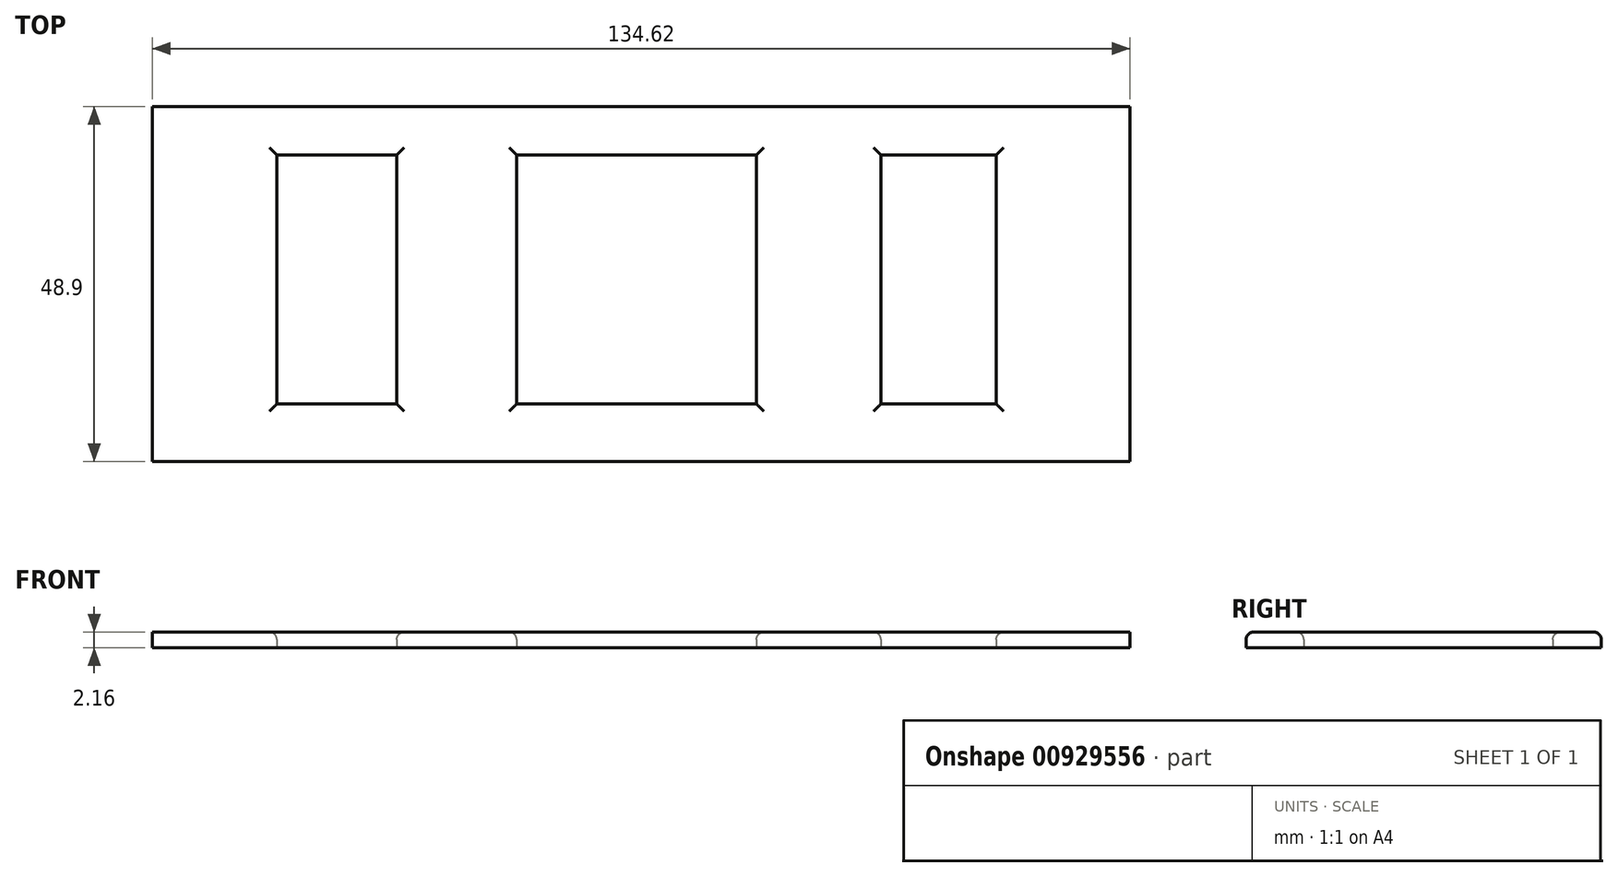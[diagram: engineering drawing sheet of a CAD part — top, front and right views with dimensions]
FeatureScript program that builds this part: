
annotation { "Feature Type Name" : "Feature", "Feature Type Description" : "" }
export const myFeature = defineFeature(function(context is Context, id is Id, definition is map)
    precondition{}
    {
        {
            var Q0;
            Q0=qCreatedBy(makeId("Top.planeOp"),FACE);
            var sketch = newSketch(context, id + "F0", { "sketchPlane" : qUnion([Q0])});
            skPoint(sketch, "E0.middle", {"position": v(0, 0) * mm});
            skLineSegment(sketch, "E1.bottom", {"start": v(-67.3, -24.45) * mm, "end": v(67.3, -24.45) * mm});
            skLineSegment(sketch, "E1.top", {"start": v(-67.3, 24.45) * mm, "end": v(67.3, 24.45) * mm});
            skLineSegment(sketch, "E1.left", {"start": v(-67.31, -24.45) * mm, "end": v(-67.3, 24.45) * mm});
            skLineSegment(sketch, "E1.right", {"start": v(67.31, -24.45) * mm, "end": v(67.31, 24.45) * mm});
            skLineSegment(sketch, "E2", {"start": v(33.02, 17.78) * mm, "end": v(33.02, -16.5) * mm});
            skLineSegment(sketch, "E3", {"start": v(67.31, 0) * mm, "end": v(67.31, 24.45) * mm});
            skLineSegment(sketch, "E4", {"start": v(67.31, 0) * mm, "end": v(67.31, -24.45) * mm});
            skLineSegment(sketch, "E5", {"start": v(-67.3, 24.45) * mm, "end": v(0, 24.45) * mm});
            skLineSegment(sketch, "E6", {"start": v(33.02, 24.45) * mm, "end": v(0, 24.45) * mm});
            skLineSegment(sketch, "E7", {"start": v(15.88, 17.78) * mm, "end": v(15.88, -16.5) * mm});
            skLineSegment(sketch, "E8", {"start": v(33.02, -24.45) * mm, "end": v(67.3, -24.45) * mm});
            skLineSegment(sketch, "E9", {"start": v(48.9, -16.5) * mm, "end": v(48.9, 17.78) * mm});
            skLineSegment(sketch, "E10", {"start": v(0, 24.45) * mm, "end": v(-67.3, 24.45) * mm});
            skLineSegment(sketch, "E11", {"start": v(-33.65, 17.78) * mm, "end": v(-33.65, -16.5) * mm});
            skLineSegment(sketch, "E12", {"start": v(-33.65, 24.45) * mm, "end": v(-67.3, 24.45) * mm});
            skLineSegment(sketch, "E13", {"start": v(-33.65, -24.45) * mm, "end": v(0, -24.45) * mm});
            skLineSegment(sketch, "E14", {"start": v(-17.14, -16.5) * mm, "end": v(-17.14, 17.78) * mm});
            skLineSegment(sketch, "E15", {"start": v(-67.31, 24.45) * mm, "end": v(-67.31, 10.48) * mm});
            skLineSegment(sketch, "E16", {"start": v(-50.16, 17.78) * mm, "end": v(-33.65, 17.78) * mm});
            skLineSegment(sketch, "E17", {"start": v(-67.31, -10.48) * mm, "end": v(-67.31, -24.45) * mm});
            skLineSegment(sketch, "E18", {"start": v(-50.16, -16.5) * mm, "end": v(-33.65, -16.5) * mm});
            skLineSegment(sketch, "E19.trimOffspring", {"start": v(-17.14, 17.78) * mm, "end": v(15.88, 17.78) * mm});
            skLineSegment(sketch, "E20.trimOffspring", {"start": v(-17.14, -16.5) * mm, "end": v(15.88, -16.5) * mm});
            skLineSegment(sketch, "E21.trimOffspring", {"start": v(33.02, 17.78) * mm, "end": v(48.9, 17.78) * mm});
            skLineSegment(sketch, "E22.trimOffspring", {"start": v(-50.16, 17.78) * mm, "end": v(-50.16, -16.5) * mm});
            skLineSegment(sketch, "E23.trimOffspring", {"start": v(33.02, -16.5) * mm, "end": v(48.9, -16.5) * mm});
            skSolve(sketch);
        }
        {
            var Q0;
            Q0=qSketchRegion(id+"F0",true);
            extrude(context, id + "F1", {"entities" : qUnion([Q0]), "depth" : 2.16 * mm, "offsetDistance" : 25.4 * mm});
        }
        {
            var Q0;
            Q0=makeQuery(id+"F1.opExtrude","CAP_EDGE",EDGE,{"disambiguationData":[OSD([sQuery(id+"F0.wireOp",EDGE,"E7")])],"isStart":false});
            var Q1;
            Q1=makeQuery(id+"F1.opExtrude","CAP_EDGE",EDGE,{"disambiguationData":[OSD([sQuery(id+"F0.wireOp",EDGE,"E11")])],"isStart":false});
            var Q2;
            Q2=makeQuery(id+"F1.opExtrude","CAP_EDGE",EDGE,{"disambiguationData":[OSD([sQuery(id+"F0.wireOp",EDGE,"E14")])],"isStart":false});
            var Q3;
            Q3=makeQuery(id+"F1.opExtrude","CAP_EDGE",EDGE,{"disambiguationData":[OSD([sQuery(id+"F0.wireOp",EDGE,"E22.trimOffspring")])],"isStart":false});
            var Q4;
            Q4=makeQuery(id+"F1.opExtrude","CAP_EDGE",EDGE,{"disambiguationData":[OSD([sQuery(id+"F0.wireOp",EDGE,"E16")])],"isStart":false});
            var Q5;
            Q5=makeQuery(id+"F1.opExtrude","CAP_EDGE",EDGE,{"disambiguationData":[OSD([sQuery(id+"F0.wireOp",EDGE,"E19.trimOffspring")])],"isStart":false});
            var Q6;
            Q6=makeQuery(id+"F1.opExtrude","CAP_EDGE",EDGE,{"disambiguationData":[OSD([sQuery(id+"F0.wireOp",EDGE,"E20.trimOffspring")])],"isStart":false});
            var Q7;
            Q7=makeQuery(id+"F1.opExtrude","CAP_EDGE",EDGE,{"disambiguationData":[OSD([sQuery(id+"F0.wireOp",EDGE,"E18")])],"isStart":false});
            var Q8;
            Q8=makeQuery(id+"F1.opExtrude","CAP_EDGE",EDGE,{"disambiguationData":[OSD([sQuery(id+"F0.wireOp",EDGE,"E23.trimOffspring")])],"isStart":false});
            var Q9;
            Q9=makeQuery(id+"F1.opExtrude","CAP_EDGE",EDGE,{"disambiguationData":[OSD([sQuery(id+"F0.wireOp",EDGE,"E2")])],"isStart":false});
            var Q10;
            Q10=makeQuery(id+"F1.opExtrude","CAP_EDGE",EDGE,{"disambiguationData":[OSD([sQuery(id+"F0.wireOp",EDGE,"E21.trimOffspring")])],"isStart":false});
            var Q11;
            Q11=makeQuery(id+"F1.opExtrude","CAP_EDGE",EDGE,{"disambiguationData":[OSD([sQuery(id+"F0.wireOp",EDGE,"E9")])],"isStart":false});
            var Q12;
            Q12=makeQuery(id+"F1.opExtrude","CAP_EDGE",EDGE,{"disambiguationData":[OSD([sQuery(id+"F0.wireOp",EDGE,"E1.bottom"),sQuery(id+"F0.wireOp",EDGE,"E8"),sQuery(id+"F0.wireOp",EDGE,"E13")])],"isStart":false});
            var Q13;
            Q13=makeQuery(id+"F1.opExtrude","CAP_EDGE",EDGE,{"disambiguationData":[OSD([sQuery(id+"F0.wireOp",EDGE,"E1.top"),sQuery(id+"F0.wireOp",EDGE,"E6"),sQuery(id+"F0.wireOp",EDGE,"E10"),sQuery(id+"F0.wireOp",EDGE,"E12")])],"isStart":false});
            var Q14;
            Q14=makeQuery(id+"F1.opExtrude","CAP_EDGE",EDGE,{"disambiguationData":[OSD([sQuery(id+"F0.wireOp",EDGE,"E3"),sQuery(id+"F0.wireOp",EDGE,"E4")])],"isStart":false});
            fillet(context, id + "F2", {"entities" : qUnion([Q0, Q1, Q2, Q3, Q4, Q5, Q6, Q7, Q8, Q9, Q10, Q11, Q12, Q13, Q14]), "radius" : 1.02 * mm, "tangentPropagation" : true, "allowEdgeOverflow" : false});
        }
    });
